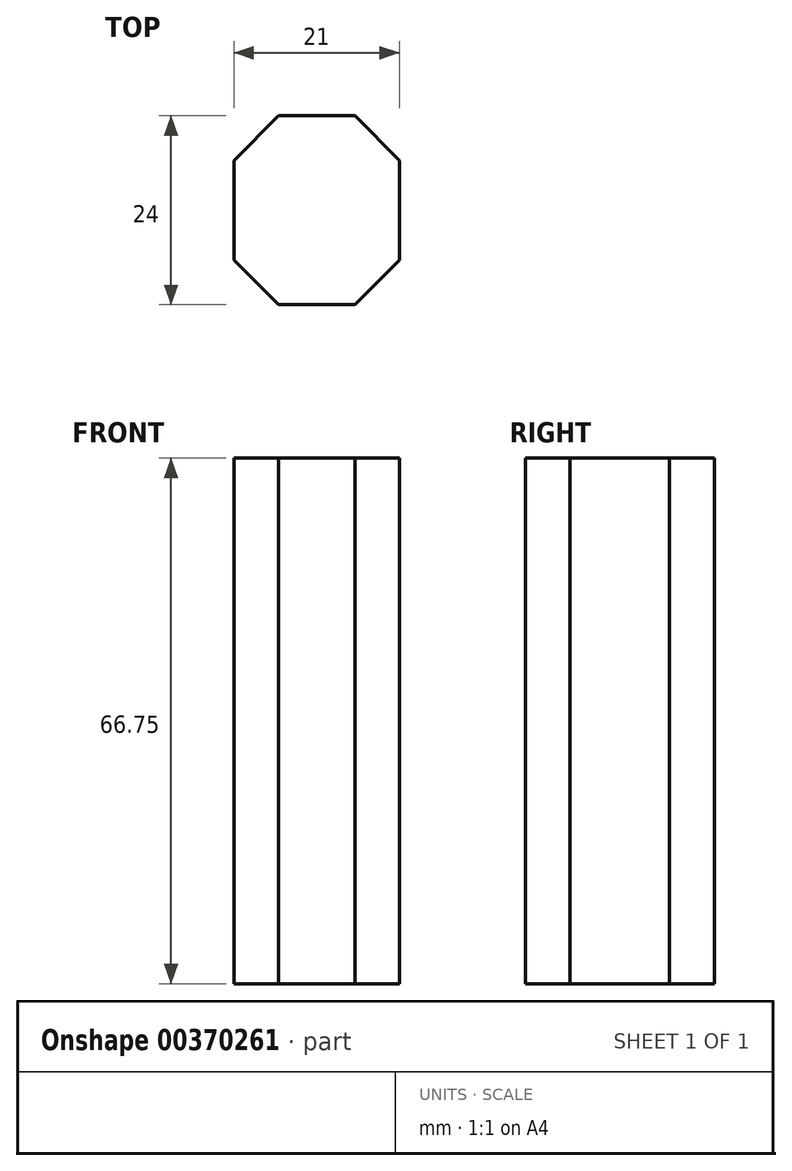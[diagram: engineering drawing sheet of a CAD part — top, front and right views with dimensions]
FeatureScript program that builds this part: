
annotation { "Feature Type Name" : "Feature", "Feature Type Description" : "" }
export const myFeature = defineFeature(function(context is Context, id is Id, definition is map)
    precondition{}
    {
        {
            var Q0;
            Q0=qCreatedBy(makeId("Top.planeOp"),FACE);
            var sketch = newSketch(context, id + "F0", { "sketchPlane" : qUnion([Q0])});
            skLineSegment(sketch, "E0.bottom", {"start": v(5.1, 12.22) * mm, "end": v(-4.58, 12.22) * mm});
            skLineSegment(sketch, "E0.top", {"start": v(5.1, -11.78) * mm, "end": v(-4.58, -11.78) * mm});
            skLineSegment(sketch, "E0.left", {"start": v(10.76, 6.56) * mm, "end": v(10.76, -6.12) * mm});
            skLineSegment(sketch, "E0.right", {"start": v(-10.24, 6.56) * mm, "end": v(-10.24, -6.12) * mm});
            skPoint(sketch, "E0.middle", {"position": v(0.26, 0.22) * mm});
            skLineSegment(sketch, "E1", {"start": v(-4.58, 12.22) * mm, "end": v(-10.24, 6.56) * mm});
            skLineSegment(sketch, "E2", {"start": v(10.76, -6.12) * mm, "end": v(5.1, -11.78) * mm});
            skLineSegment(sketch, "E3", {"start": v(5.1, 12.22) * mm, "end": v(10.76, 6.56) * mm});
            skLineSegment(sketch, "E4", {"start": v(-10.24, -6.12) * mm, "end": v(-4.58, -11.78) * mm});
            skSolve(sketch);
        }
        {
            var Q0;
            Q0 = qSketchRegion(id + "F0", true);
            extrude(context, id + "F1", {"entities" : qUnion([Q0]), "depth" : 66.75 * mm});
        }
    });
